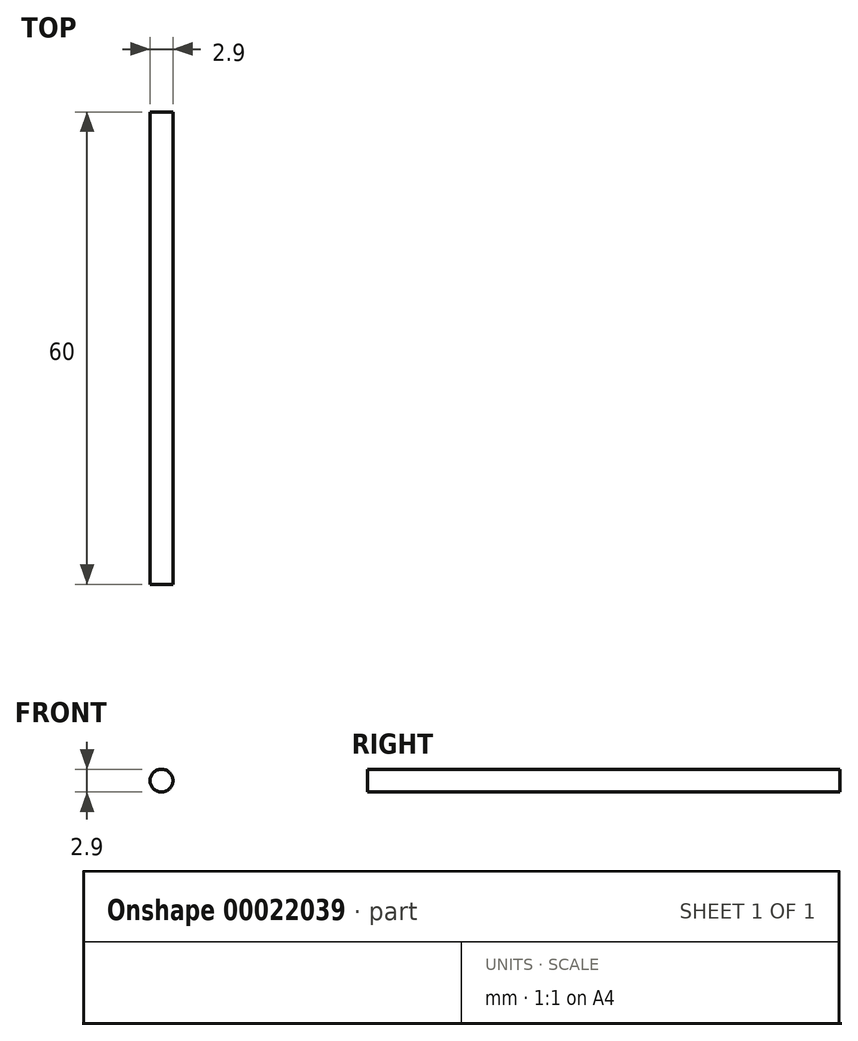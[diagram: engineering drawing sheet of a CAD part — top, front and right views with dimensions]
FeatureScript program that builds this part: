
annotation { "Feature Type Name" : "Feature", "Feature Type Description" : "" }
export const myFeature = defineFeature(function(context is Context, id is Id, definition is map)
    precondition{}
    {
        {
            var Q0;
            Q0=qCreatedBy(makeId("Front.planeOp"),FACE);
            var sketch = newSketch(context, id + "F0", { "sketchPlane" : qUnion([Q0])});
            skCircle(sketch, "E0", {"center": v(-35.72, 4.38) * mm, "radius": 1.45 * mm});
            skSolve(sketch);
        }
        {
            var Q0;
            Q0=makeQuery(id+"F0.imprint","IMPRINT",FACE,{"disambiguationData":[TD([[makeQuery(id+"F0.imprint","IMPRINT",EDGE,{"derivedFrom":sQuery(id+"F0.wireOp",EDGE,"E0")}),1.0]])]});
            extrude(context, id + "F1", {"entities" : qUnion([Q0]), "depth" : 30 * mm});
        }
        {
            var Q0;
            Q0=makeQuery(id+"F1.opExtrude","SWEPT_BODY",BODY,{"disambiguationData":[OSD([sQuery(id+"F0.wireOp",EDGE,"E0")])]});
            var Q1;
            Q1=qCreatedBy(makeId("Front.planeOp"),FACE);
            mirror(context, id + "F2", {"operationType" : NewBodyOperationType.ADD, "entities" : qUnion([Q0]), "mirrorPlane" : qUnion([Q1])});
        }
    });
